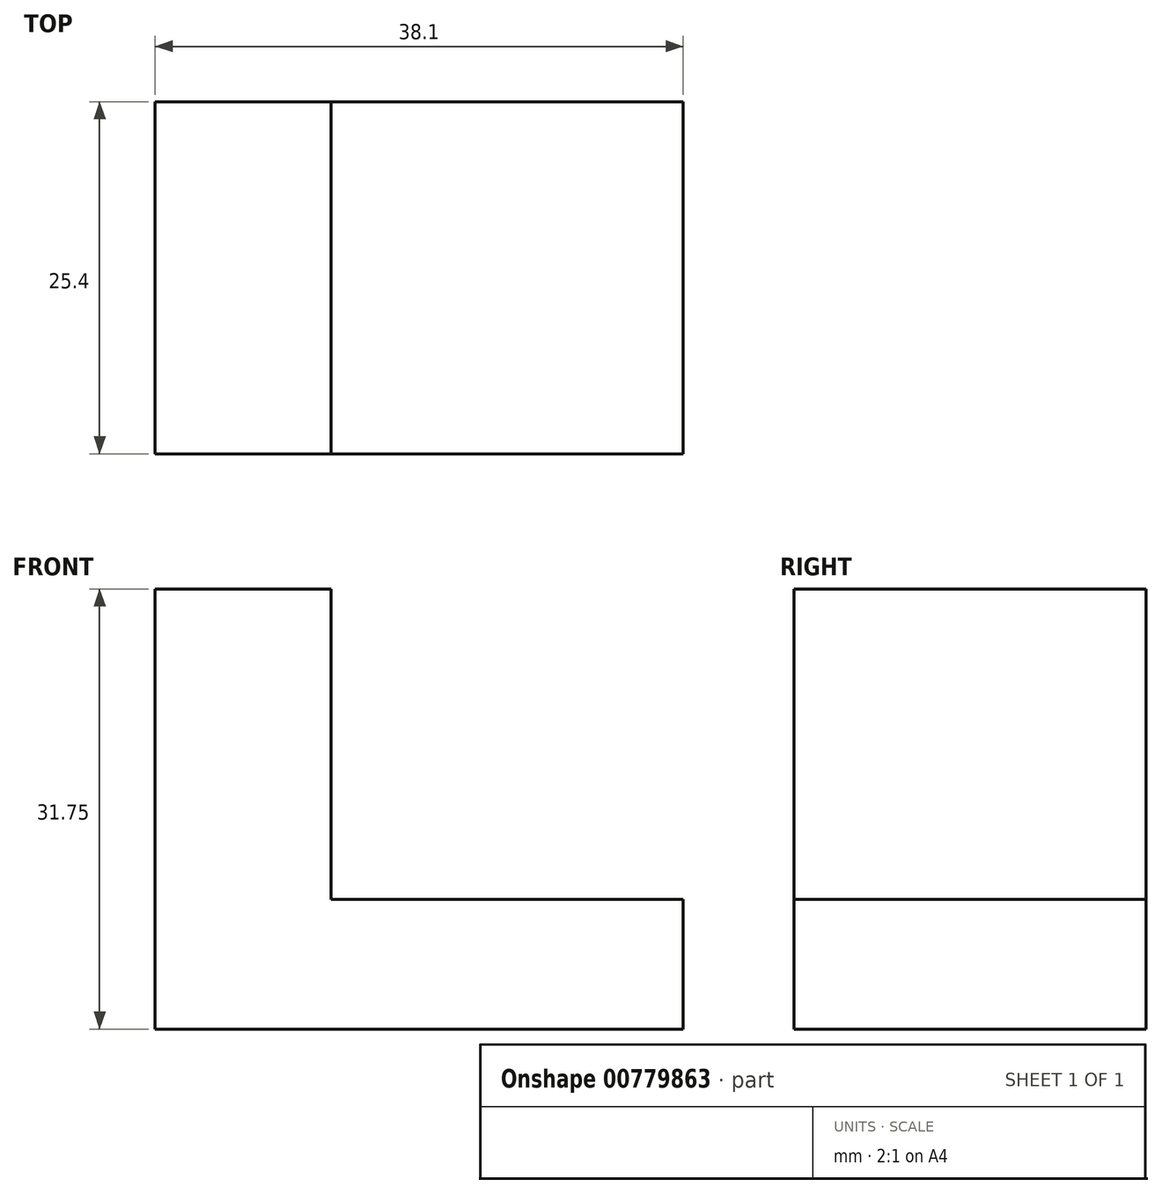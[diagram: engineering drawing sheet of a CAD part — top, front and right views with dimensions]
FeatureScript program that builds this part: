
annotation { "Feature Type Name" : "Feature", "Feature Type Description" : "" }
export const myFeature = defineFeature(function(context is Context, id is Id, definition is map)
    precondition{}
    {
        {
            var Q0;
            Q0=qCreatedBy(makeId("Front.planeOp"),FACE);
            var sketch = newSketch(context, id + "F0", { "sketchPlane" : qUnion([Q0])});
            skLineSegment(sketch, "E0", {"start": v(0, 0) * mm, "end": v(0, 31.75) * mm});
            skLineSegment(sketch, "E1", {"start": v(0, 31.75) * mm, "end": v(38.1, 31.75) * mm});
            skLineSegment(sketch, "E2", {"start": v(38.1, 31.75) * mm, "end": v(38.1, 0) * mm});
            skLineSegment(sketch, "E3", {"start": v(38.1, 0) * mm, "end": v(0, 0) * mm});
            skSolve(sketch);
        }
        {
            var Q0;
            Q0=makeQuery(id+"F0.imprint","IMPRINT",FACE,{"disambiguationData":[TD([[makeQuery(id+"F0.imprint","IMPRINT",EDGE,{"derivedFrom":sQuery(id+"F0.wireOp",EDGE,"E0")}),-1.0]])]});
            extrude(context, id + "F1", {"entities" : qUnion([Q0]), "depth" : 25.4 * mm, "offsetDistance" : 25.4 * mm});
        }
        {
            var Q0;
            Q0=makeQuery(id+"F1.opExtrude","CAP_FACE",FACE,{"disambiguationData":[OSD([sQuery(id+"F0.wireOp",EDGE,"E0"),sQuery(id+"F0.wireOp",EDGE,"E1"),sQuery(id+"F0.wireOp",EDGE,"E2"),sQuery(id+"F0.wireOp",EDGE,"E3")])],"isStart":false});
            var sketch = newSketch(context, id + "F2", { "sketchPlane" : qUnion([Q0])});
            skLineSegment(sketch, "E4", {"start": v(0, 31.75) * mm, "end": v(0, 0) * mm});
            skLineSegment(sketch, "E5", {"start": v(0, 0) * mm, "end": v(38.1, 0) * mm});
            skLineSegment(sketch, "E6", {"start": v(38.1, 0) * mm, "end": v(38.1, 9.35) * mm});
            skLineSegment(sketch, "E7", {"start": v(38.1, 9.35) * mm, "end": v(12.7, 9.35) * mm});
            skLineSegment(sketch, "E8", {"start": v(12.7, 9.35) * mm, "end": v(12.7, 31.75) * mm});
            skLineSegment(sketch, "E9", {"start": v(12.7, 31.75) * mm, "end": v(0, 31.75) * mm});
            skSolve(sketch);
        }
        {
            var Q0;
            Q0=qCreatedBy(makeId("Front.planeOp"),FACE);
            var sketch = newSketch(context, id + "F3", { "sketchPlane" : qUnion([Q0])});
            skSolve(sketch);
        }
        {
            var Q0;
            Q0 = qSketchRegion(id + "F3", true);
            var Q1;
            {var subQ0=sQuery(id+"F2.wireOp",EDGE,"E7");Q1=makeQuery(id+"F2.imprint","IMPRINT",FACE,{"disambiguationData":[TD([[makeQuery(id+"F2.imprint","IMPRINT",EDGE,{"derivedFrom":subQ0}),-1.0]])]});}
            extrude(context, id + "F4", {"entities" : qUnion([Q0, Q1]), "operationType" : NewBodyOperationType.REMOVE, "endBound" : BoundingType.THROUGH_ALL, "oppositeDirection" : true, "depth" : 25.4 * mm, "offsetDistance" : 25.4 * mm});
        }
    });
